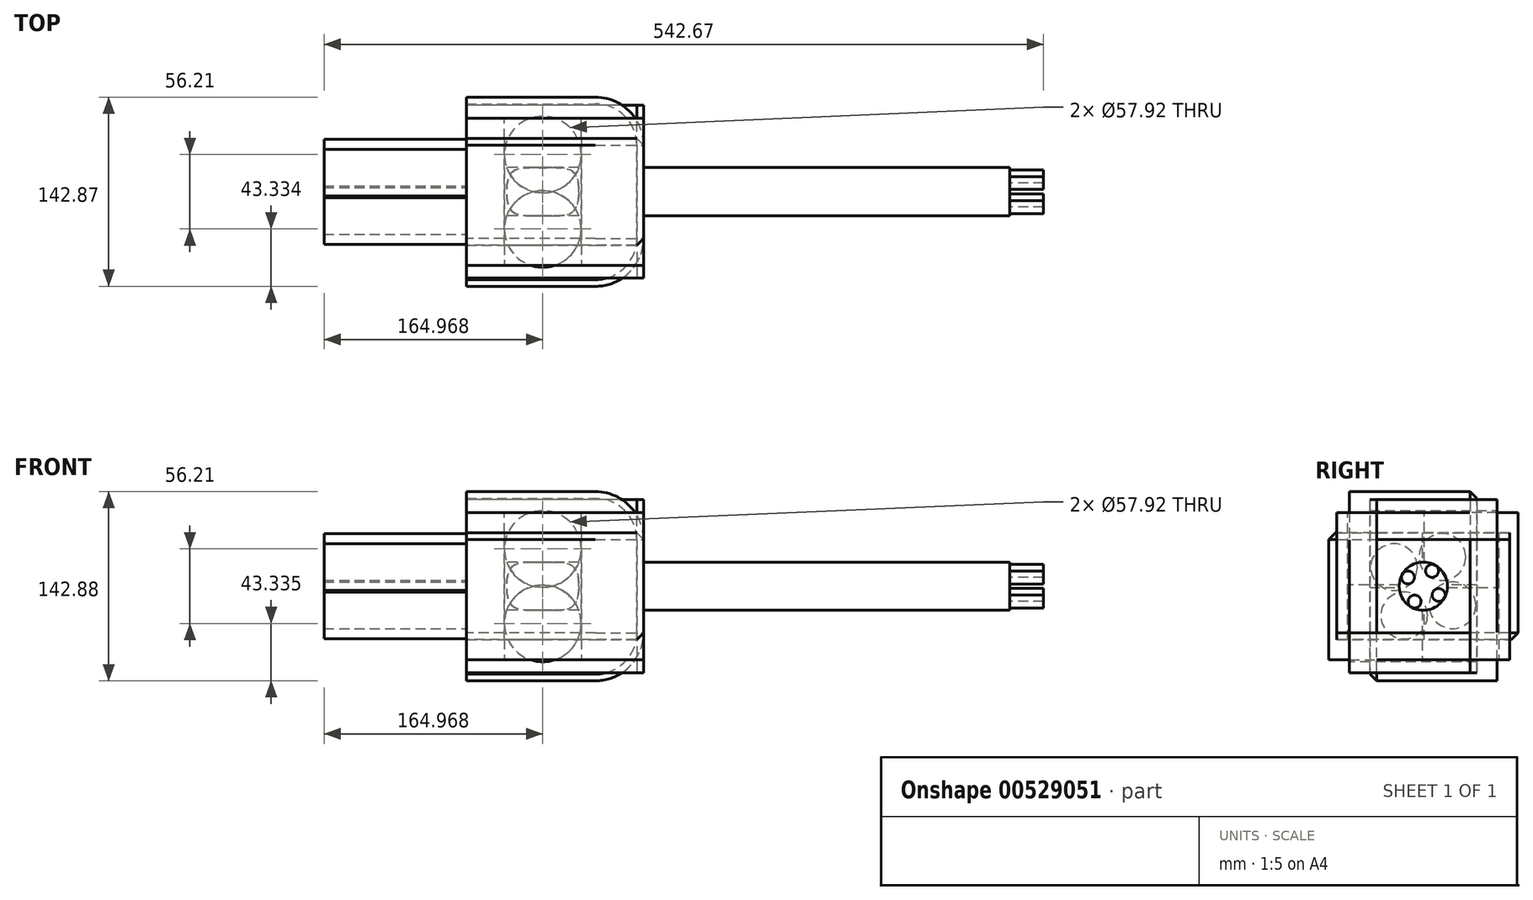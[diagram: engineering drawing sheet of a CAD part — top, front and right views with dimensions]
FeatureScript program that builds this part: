
annotation { "Feature Type Name" : "Feature", "Feature Type Description" : "" }
export const myFeature = defineFeature(function(context is Context, id is Id, definition is map)
    precondition{}
    {
        {
            var Q0;
            Q0=qCreatedBy(makeId("Front.planeOp"),FACE);
            var sketch = newSketch(context, id + "F0", { "sketchPlane" : qUnion([Q0])});
            skLineSegment(sketch, "E0.bottom", {"start": v(45.02, 65.27) * mm, "end": v(-88.6, 65.27) * mm});
            skLineSegment(sketch, "E0.top", {"start": v(45.02, -71.44) * mm, "end": v(-88.6, -71.44) * mm});
            skLineSegment(sketch, "E0.left", {"start": v(45.02, 65.27) * mm, "end": v(45.02, -71.44) * mm});
            skLineSegment(sketch, "E0.right", {"start": v(-88.6, 65.27) * mm, "end": v(-88.6, -71.44) * mm});
            skCircle(sketch, "E1", {"center": v(-31.07, 28.1) * mm, "radius": 28.96 * mm});
            skSolve(sketch);
        }
        {
            var Q0;
            Q0=makeQuery(id+"F0.imprint","IMPRINT",FACE,{"disambiguationData":[TD([[makeQuery(id+"F0.imprint","IMPRINT",EDGE,{"derivedFrom":sQuery(id+"F0.wireOp",EDGE,"E0.bottom")}),1.0]])]});
            extrude(context, id + "F1", {"entities" : qUnion([Q0]), "depth" : 96.02 * mm, "offsetDistance" : 25.4 * mm});
        }
        {
            var Q0;
            Q0=makeQuery(id+"F1.opExtrude","SWEPT_FACE",FACE,{"disambiguationData":[OSD([sQuery(id+"F0.wireOp",EDGE,"E0.right")])]});
            var sketch = newSketch(context, id + "F2", { "sketchPlane" : qUnion([Q0])});
            skCircle(sketch, "E2", {"center": v(55.64, 0) * mm, "radius": 18.2 * mm});
            skSolve(sketch);
        }
        {
            var Q0;
            Q0=makeQuery(id+"F2.imprint","IMPRINT",FACE,{"disambiguationData":[TD([[makeQuery(id+"F2.imprint","IMPRINT",EDGE,{"derivedFrom":sQuery(id+"F2.wireOp",EDGE,"E2")}),1.0]])]});
            extrude(context, id + "F3", {"entities" : qUnion([Q0]), "operationType" : NewBodyOperationType.ADD, "oppositeDirection" : true, "depth" : 409.82 * mm, "offsetDistance" : 25.4 * mm});
        }
        {
            var Q0;
            Q0=makeQuery(id+"F1.opExtrude","SWEPT_EDGE",EDGE,{"disambiguationData":[OSD([sQuery(id+"F0.wireOp",EDGE,"E0.top"),sQuery(id+"F0.wireOp",EDGE,"E0.left")])]});
            fillet(context, id + "F4", {"entities" : qUnion([Q0]), "radius" : 36.4 * mm, "tangentPropagation" : true, "allowEdgeOverflow" : false});
        }
        {
            var Q0;
            Q0=makeQuery(id+"F1.opExtrude","SWEPT_FACE",FACE,{"disambiguationData":[OSD([sQuery(id+"F0.wireOp",EDGE,"E0.right")])]});
            var sketch = newSketch(context, id + "F5", { "sketchPlane" : qUnion([Q0])});
            skCircle(sketch, "E3", {"center": v(33.58, -14.42) * mm, "radius": 17.6 * mm});
            skSolve(sketch);
        }
        {
            var Q0;
            Q0=makeQuery(id+"F5.imprint","IMPRINT",FACE,{"disambiguationData":[TD([[makeQuery(id+"F5.imprint","IMPRINT",EDGE,{"derivedFrom":sQuery(id+"F5.wireOp",EDGE,"E3")}),1.0]])]});
            extrude(context, id + "F6", {"entities" : qUnion([Q0]), "operationType" : NewBodyOperationType.ADD, "depth" : 107.45 * mm, "offsetDistance" : 25.4 * mm});
        }
        {
            var Q0;
            Q0=makeQuery(id+"F1.opExtrude","CAP_EDGE",EDGE,{"disambiguationData":[OSD([sQuery(id+"F0.wireOp",EDGE,"E0.top")])],"isStart":false});
            chamfer(context, id + "F7", {"entities" : qUnion([Q0]), "width" : 5.08 * mm, "tangentPropagation" : true});
        }
        {
            var Q0;
            Q0=makeQuery(id+"F3.opExtrude","CAP_FACE",FACE,{"disambiguationData":[OSD([sQuery(id+"F2.wireOp",EDGE,"E2")])],"isStart":false});
            var sketch = newSketch(context, id + "F8", { "sketchPlane" : qUnion([Q0])});
            skCircle(sketch, "E4", {"center": v(-49.04, 11.6) * mm, "radius": 4.87 * mm});
            skSolve(sketch);
        }
        {
            var Q0;
            Q0=makeQuery(id+"F8.imprint","IMPRINT",FACE,{"disambiguationData":[TD([[makeQuery(id+"F8.imprint","IMPRINT",EDGE,{"derivedFrom":sQuery(id+"F8.wireOp",EDGE,"E4")}),1.0]])]});
            extrude(context, id + "F9", {"entities" : qUnion([Q0]), "operationType" : NewBodyOperationType.ADD, "depth" : 25.4 * mm, "offsetDistance" : 25.4 * mm});
        }
        {
            var Q0;
            Q0=makeQuery(id+"F1.opExtrude","SWEPT_BODY",BODY,{"disambiguationData":[OSD([sQuery(id+"F0.wireOp",EDGE,"E0.bottom"),sQuery(id+"F0.wireOp",EDGE,"E0.top"),sQuery(id+"F0.wireOp",EDGE,"E0.left"),sQuery(id+"F0.wireOp",EDGE,"E0.right"),sQuery(id+"F0.wireOp",EDGE,"E1")])]});
            var Q1;
            {var subQ0=sQuery(id+"F2.wireOp",EDGE,"E2");Q1=makeQuery(id+"F3.boolean.opBoolean","SPLIT",FACE,{"disambiguationData":[TD([makeQuery(id+"F1.opExtrude","SWEPT_FACE",FACE,{"disambiguationData":[OSD([sQuery(id+"F0.wireOp",EDGE,"E0.left")])]})])],"derivedFrom":makeQuery(id+"F3.opExtrude","SWEPT_FACE",FACE,{"disambiguationData":[OSD([subQ0])]})});}
            circularPattern(context, id + "F10", {"entities" : qUnion([Q0]), "axis" : qUnion([Q1]), "angle" : 360 * degree, "instanceCount" : 4, "equalSpace" : true});
        }
    });
